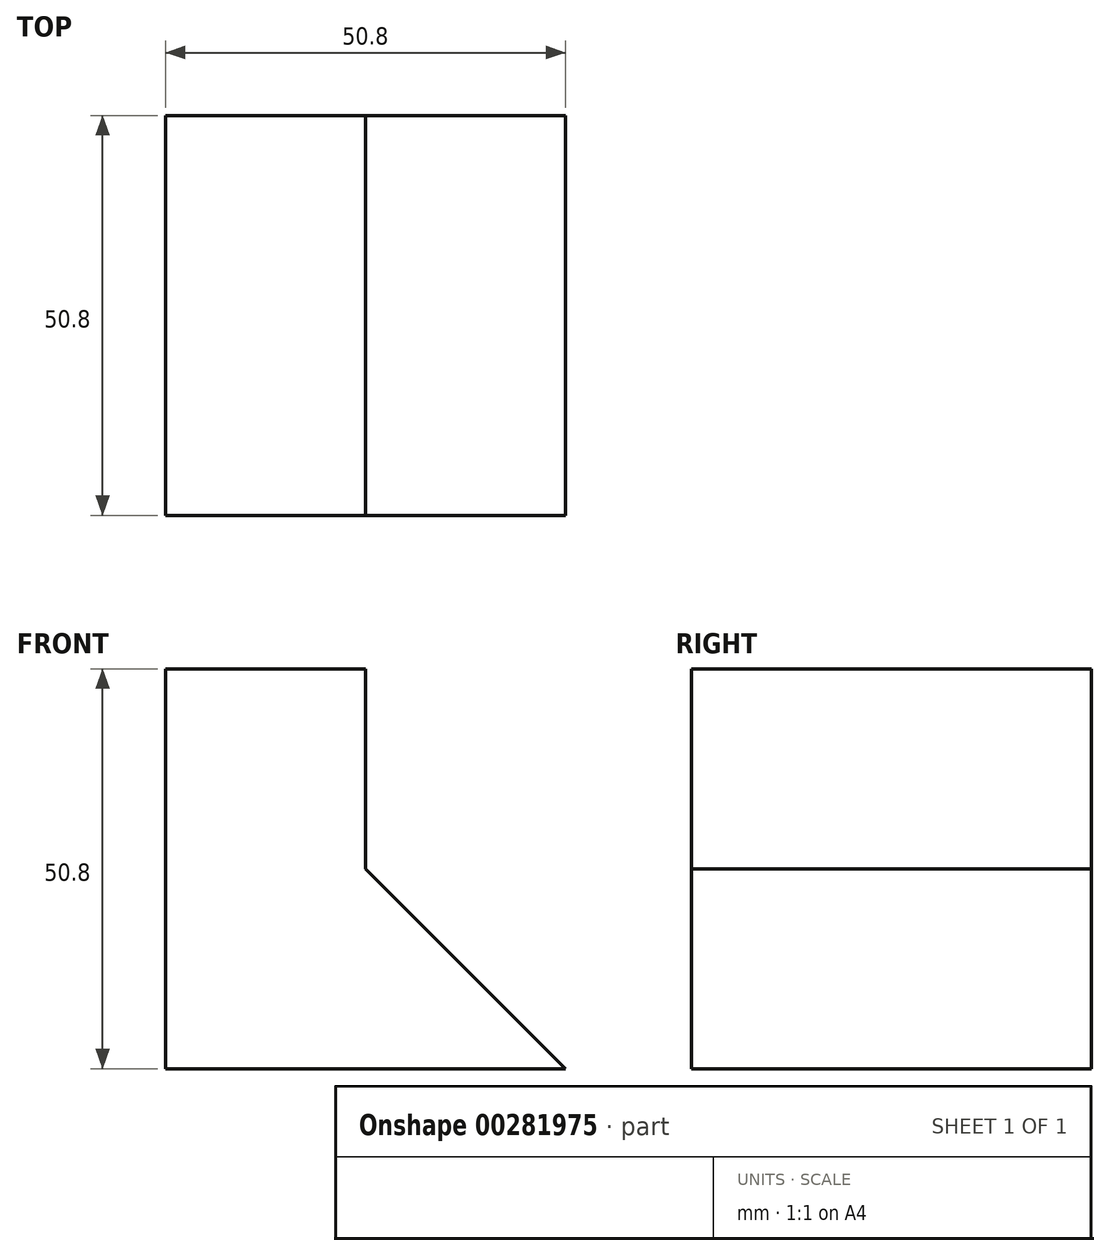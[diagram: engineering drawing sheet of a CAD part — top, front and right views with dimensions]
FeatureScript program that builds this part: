
annotation { "Feature Type Name" : "Feature", "Feature Type Description" : "" }
export const myFeature = defineFeature(function(context is Context, id is Id, definition is map)
    precondition{}
    {
        {
            var Q0;
            Q0=qCreatedBy(makeId("Front.planeOp"),FACE);
            var sketch = newSketch(context, id + "F0", { "sketchPlane" : qUnion([Q0])});
            skLineSegment(sketch, "E0", {"start": v(-50.8, 75.05) * mm, "end": v(-50.8, 24.25) * mm});
            skLineSegment(sketch, "E1", {"start": v(-50.8, 24.25) * mm, "end": v(0, 24.25) * mm});
            skLineSegment(sketch, "E2", {"start": v(0, 24.25) * mm, "end": v(-50.8, 24.25) * mm});
            skLineSegment(sketch, "E3", {"start": v(-50.8, 75.05) * mm, "end": v(-25.4, 75.05) * mm});
            skLineSegment(sketch, "E4", {"start": v(-25.4, 75.05) * mm, "end": v(-25.4, 49.65) * mm});
            skLineSegment(sketch, "E5", {"start": v(-25.4, 49.65) * mm, "end": v(0, 24.25) * mm});
            skSolve(sketch);
        }
        {
            var Q0;
            Q0 = qSketchRegion(id + "F0", true);
            extrude(context, id + "F1", {"entities" : qUnion([Q0]), "depth" : 50.8 * mm});
        }
    });
